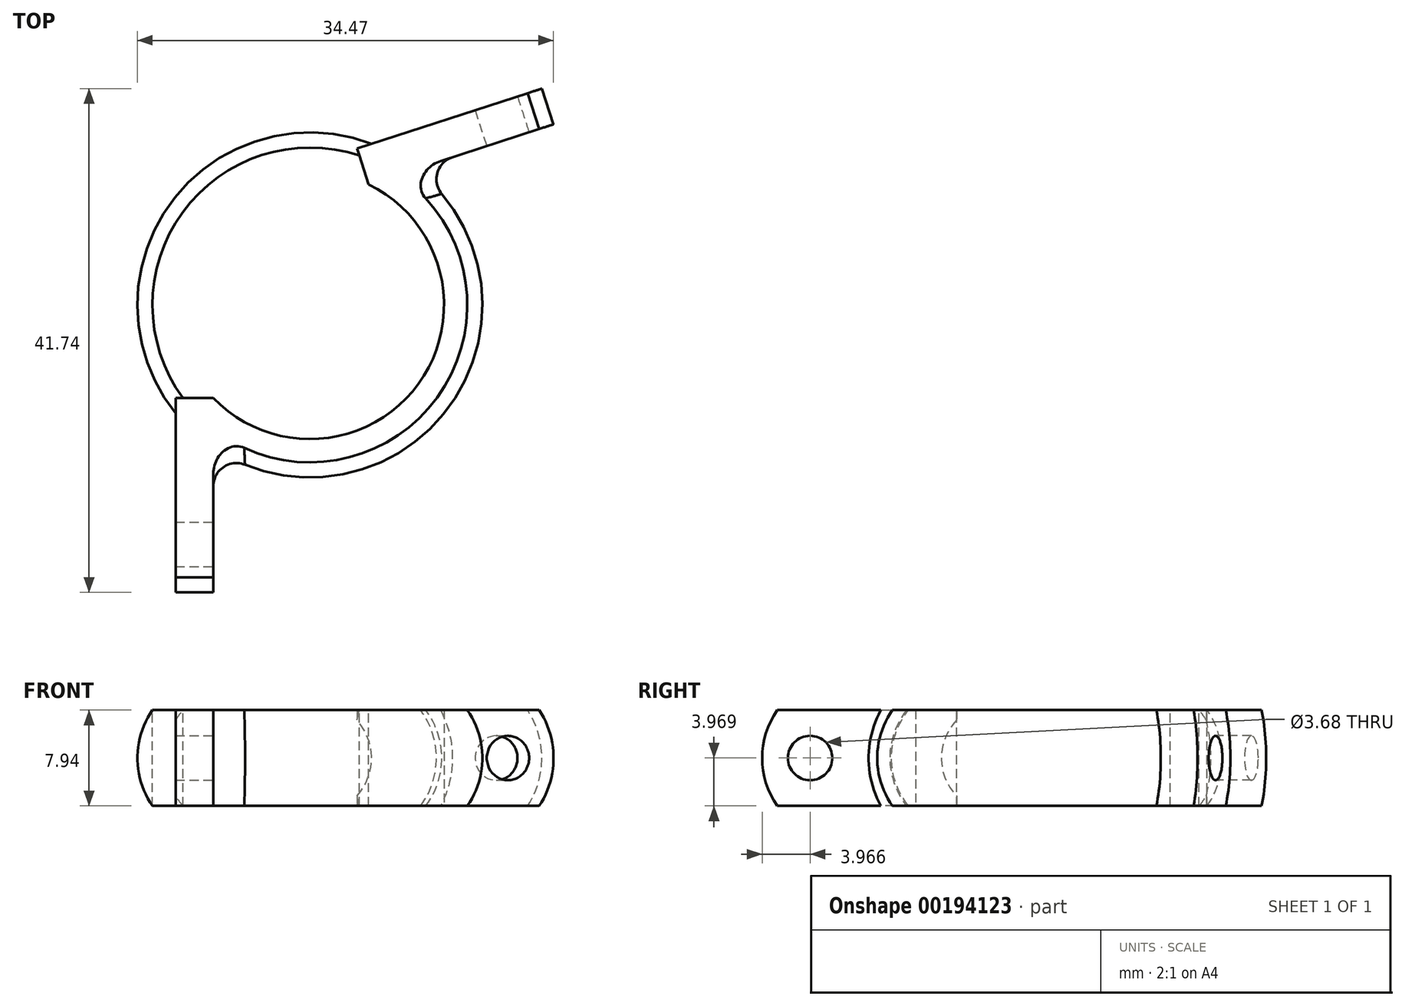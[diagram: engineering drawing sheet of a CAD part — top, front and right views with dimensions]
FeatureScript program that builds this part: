
annotation { "Feature Type Name" : "Feature", "Feature Type Description" : "" }
export const myFeature = defineFeature(function(context is Context, id is Id, definition is map)
    precondition{}
    {
        {
            var Q0;
            Q0=qCreatedBy(makeId("Top.planeOp"),FACE);
            var sketch = newSketch(context, id + "F0", { "sketchPlane" : qUnion([Q0])});
            skCircle(sketch, "E0", {"center": v(0, 0) * mm, "radius": 11.11 * mm, "construction": true});
            skLineSegment(sketch, "E1", {"start": v(-11.11, -27.21) * mm, "end": v(-11.11, 8.07) * mm, "construction": true});
            skLineSegment(sketch, "E2", {"start": v(-11.11, 8.07) * mm, "end": v(23.14, 19.2) * mm, "construction": true});
            skSolve(sketch);
        }
        {
            var Q0;
            Q0=qCreatedBy(makeId("Front.planeOp"),FACE);
            var sketch = newSketch(context, id + "F1", { "sketchPlane" : qUnion([Q0])});
            skLineSegment(sketch, "E3", {"start": v(-13.04, 0) * mm, "end": v(-11.11, 0) * mm});
            skLineSegment(sketch, "E4", {"start": v(-11.11, 0) * mm, "end": v(-11.11, 7.94) * mm});
            skLineSegment(sketch, "E5", {"start": v(-11.11, 7.94) * mm, "end": v(-13.04, 7.94) * mm});
            skArc(sketch, "E6", {"start": v(-13.04, 7.94) * mm, "mid": v(-14.29, 3.97) * mm, "end": v(-13.04, 0) * mm});
            skLineSegment(sketch, "E7", {"start": v(-13.04, 0) * mm, "end": v(-15.82, 3.97) * mm, "construction": true});
            skLineSegment(sketch, "E8", {"start": v(-13.04, 7.94) * mm, "end": v(-13.04, 0) * mm, "construction": true});
            skLineSegment(sketch, "E9", {"start": v(0, 0) * mm, "end": v(0, 7.94) * mm, "construction": true});
            skSolve(sketch);
        }
        {
            var Q0;
            Q0=makeQuery(id+"F1.imprint","IMPRINT",FACE,{"disambiguationData":[TD([[makeQuery(id+"F1.imprint","IMPRINT",EDGE,{"derivedFrom":sQuery(id+"F1.wireOp",EDGE,"E3")}),1.0]])]});
            var Q1;
            Q1=sQuery(id+"F1.wireOp",EDGE,"E9");
            revolve(context, id + "F2", {"entities" : qUnion([Q0]), "axis" : qUnion([Q1]), "revolveType" : RevolveType.FULL});
        }
        {
            var Q0;
            Q0=makeQuery(id+"F2.opRevolve","SWEPT_FACE",FACE,{"disambiguationData":[OSD([sQuery(id+"F1.wireOp",EDGE,"E5")])]});
            var sketch = newSketch(context, id + "F3", { "sketchPlane" : qUnion([Q0])});
            skLineSegment(sketch, "E10", {"start": v(-6.53, -9) * mm, "end": v(6.53, 9) * mm, "construction": true});
            skLineSegment(sketch, "E11", {"start": v(0, 0) * mm, "end": v(-11.11, 8.07) * mm, "construction": true});
            skLineSegment(sketch, "E12", {"start": v(4.87, 9.99) * mm, "end": v(0, 0) * mm, "construction": true});
            skLineSegment(sketch, "E13", {"start": v(0, 0) * mm, "end": v(-8, -7.72) * mm, "construction": true});
            skArc(sketch, "E14", {"start": v(-8, -7.72) * mm, "mid": v(-9, 6.53) * mm, "end": v(4.87, 9.99) * mm});
            skArc(sketch, "E15", {"start": v(-10.28, -9.92) * mm, "mid": v(-11.56, 8.4) * mm, "end": v(6.26, 12.84) * mm});
            skLineSegment(sketch, "E16", {"start": v(6.26, 12.84) * mm, "end": v(4.87, 9.99) * mm});
            skLineSegment(sketch, "E17", {"start": v(-8, -7.72) * mm, "end": v(-10.28, -9.92) * mm});
            skSolve(sketch);
        }
        {
            var Q0;
            {var subQ0=sQuery(id+"F3.wireOp",EDGE,"E15");Q0=makeQuery(id+"F3.imprint","IMPRINT",FACE,{"disambiguationData":[TD([[makeQuery(id+"F3.imprint","IMPRINT",EDGE,{"derivedFrom":subQ0}),-1.0]])]});}
            var Q1;
            {var subQ0=sQuery(id+"F3.wireOp",EDGE,"E14");Q1=makeQuery(id+"F3.imprint","IMPRINT",FACE,{"disambiguationData":[TD([[makeQuery(id+"F3.imprint","IMPRINT",EDGE,{"derivedFrom":subQ0}),1.0]])]});}
            extrude(context, id + "F4", {"entities" : qUnion([Q0, Q1]), "operationType" : NewBodyOperationType.REMOVE, "endBound" : BoundingType.UP_TO_NEXT, "oppositeDirection" : true, "depth" : 25.4 * mm});
        }
        {
            var Q0;
            Q0=qCreatedBy(makeId("Top.planeOp"),FACE);
            var sketch = newSketch(context, id + "F5", { "sketchPlane" : qUnion([Q0])});
            skCircle(sketch, "E18", {"center": v(0, 0) * mm, "radius": 14.29 * mm, "construction": true});
            skLineSegment(sketch, "E19.bottom", {"start": v(-11.11, -7.72) * mm, "end": v(-8, -7.72) * mm});
            skLineSegment(sketch, "E19.top", {"start": v(-11.11, -23.81) * mm, "end": v(-8, -23.81) * mm});
            skLineSegment(sketch, "E19.left", {"start": v(-11.11, -7.72) * mm, "end": v(-11.11, -23.81) * mm});
            skLineSegment(sketch, "E19.right", {"start": v(-8, -7.72) * mm, "end": v(-8, -23.81) * mm});
            skLineSegment(sketch, "E20", {"start": v(19.21, 17.93) * mm, "end": v(3.9, 12.95) * mm});
            skLineSegment(sketch, "E21", {"start": v(3.9, 12.95) * mm, "end": v(4.87, 9.99) * mm});
            skLineSegment(sketch, "E22", {"start": v(4.87, 9.99) * mm, "end": v(20.18, 14.96) * mm});
            skLineSegment(sketch, "E23", {"start": v(20.18, 14.96) * mm, "end": v(19.21, 17.93) * mm});
            skLineSegment(sketch, "E24", {"start": v(13.59, 4.42) * mm, "end": v(11.12, 12.02) * mm, "construction": true});
            skLineSegment(sketch, "E25", {"start": v(0, -14.29) * mm, "end": v(-8, -14.29) * mm, "construction": true});
            skLineSegment(sketch, "E26", {"start": v(0, -14.29) * mm, "end": v(0, -13.04) * mm, "construction": true});
            skLineSegment(sketch, "E27", {"start": v(13.59, 4.42) * mm, "end": v(12.4, 4.03) * mm, "construction": true});
            skSolve(sketch);
        }
        {
            var Q0;
            Q0=makeQuery(id+"F5.imprint","IMPRINT",FACE,{"disambiguationData":[TD([[makeQuery(id+"F5.imprint","IMPRINT",EDGE,{"derivedFrom":sQuery(id+"F5.wireOp",EDGE,"E19.bottom")}),-1.0]])]});
            var Q1;
            Q1=makeQuery(id+"F5.imprint","IMPRINT",FACE,{"disambiguationData":[TD([[makeQuery(id+"F5.imprint","IMPRINT",EDGE,{"derivedFrom":sQuery(id+"F5.wireOp",EDGE,"E20")}),1.0]])]});
            var Q2;
            Q2=makeQuery(id+"F2.opRevolve","SWEPT_FACE",FACE,{"disambiguationData":[OSD([sQuery(id+"F1.wireOp",EDGE,"E5")])]});
            extrude(context, id + "F6", {"entities" : qUnion([Q0, Q1]), "operationType" : NewBodyOperationType.ADD, "endBound" : BoundingType.UP_TO_SURFACE, "endBoundEntityFace" : qUnion([Q2]), "depth" : 25.4 * mm});
        }
        {
            var Q0;
            Q0=makeQuery(id+"F6.opExtrude","SWEPT_FACE",FACE,{"disambiguationData":[OSD([sQuery(id+"F5.wireOp",EDGE,"E19.right")])]});
            var sketch = newSketch(context, id + "F7", { "sketchPlane" : qUnion([Q0])});
            skCircle(sketch, "E28", {"center": v(-19.84, 3.97) * mm, "radius": 3.97 * mm, "construction": true});
            skCircle(sketch, "E29", {"center": v(-19.84, 3.97) * mm, "radius": 1.84 * mm});
            skLineSegment(sketch, "E30", {"start": v(-13.04, 0) * mm, "end": v(-13.04, 7.94) * mm, "construction": true});
            skLineSegment(sketch, "E31", {"start": v(-14.29, 7.94) * mm, "end": v(-14.29, 0) * mm, "construction": true});
            skArc(sketch, "E32", {"start": v(-13.04, 7.94) * mm, "mid": v(-14.29, 3.97) * mm, "end": v(-13.04, 0) * mm});
            skArc(sketch, "E33", {"start": v(-10.3, 7.94) * mm, "mid": v(-11.84, 3.97) * mm, "end": v(-10.3, 0) * mm});
            skArc(sketch, "E34", {"start": v(-22.56, 7.94) * mm, "mid": v(-23.81, 3.97) * mm, "end": v(-22.56, 0) * mm});
            skLineSegment(sketch, "E35", {"start": v(-10.3, 7.94) * mm, "end": v(-13.04, 7.94) * mm});
            skLineSegment(sketch, "E36", {"start": v(-10.3, 0) * mm, "end": v(-13.04, 0) * mm});
            skSolve(sketch);
        }
        {
            var Q0;
            {var subQ0=sQuery(id+"F7.wireOp",EDGE,"E34");var subQ1=sQuery(id+"F5.wireOp",EDGE,"E19.right");var subQ2=makeQuery(id+"F6.opExtrude","CAP_EDGE",EDGE,{"disambiguationData":[OSD([subQ1])],"isStart":false});var subQ3=makeQuery(id+"F7.imprint","INTERSECT",VERTEX,{"derivedFrom":[subQ2,subQ0]});Q0=makeQuery(id+"F7.imprint","IMPRINT",FACE,{"disambiguationData":[TD([[makeQuery(id+"F7.imprint","IMPRINT",EDGE,{"disambiguationData":[TD([[subQ3,-1.0]])],"derivedFrom":subQ0}),-1.0]])]});}
            var Q1;
            {var subQ0=sQuery(id+"F7.wireOp",EDGE,"E34");var subQ1=sQuery(id+"F5.wireOp",EDGE,"E19.right");var subQ2=makeQuery(id+"F6.opExtrude","CAP_EDGE",EDGE,{"disambiguationData":[OSD([subQ1])],"isStart":true});var subQ3=makeQuery(id+"F7.imprint","INTERSECT",VERTEX,{"derivedFrom":[subQ2,subQ0]});Q1=makeQuery(id+"F7.imprint","IMPRINT",FACE,{"disambiguationData":[TD([[makeQuery(id+"F7.imprint","IMPRINT",EDGE,{"disambiguationData":[TD([[subQ3,1.0]])],"derivedFrom":subQ0}),-1.0]])]});}
            var Q2;
            Q2=makeQuery(id+"F7.imprint","IMPRINT",FACE,{"disambiguationData":[TD([[makeQuery(id+"F7.imprint","IMPRINT",EDGE,{"derivedFrom":sQuery(id+"F7.wireOp",EDGE,"E29")}),1.0]])]});
            extrude(context, id + "F8", {"entities" : qUnion([Q0, Q1, Q2]), "operationType" : NewBodyOperationType.REMOVE, "endBound" : BoundingType.UP_TO_NEXT, "oppositeDirection" : true, "depth" : 25.4 * mm});
        }
        {
            var Q0;
            Q0=makeQuery(id+"F6.opExtrude","SWEPT_FACE",FACE,{"disambiguationData":[OSD([sQuery(id+"F5.wireOp",EDGE,"E22")])]});
            var sketch = newSketch(context, id + "F9", { "sketchPlane" : qUnion([Q0])});
            skLineSegment(sketch, "E37", {"start": v(14.29, 0) * mm, "end": v(14.29, 7.94) * mm, "construction": true});
            skLineSegment(sketch, "E38", {"start": v(13.04, 0) * mm, "end": v(13.04, 7.94) * mm, "construction": true});
            skArc(sketch, "E39", {"start": v(13.04, 0) * mm, "mid": v(14.29, 3.97) * mm, "end": v(13.04, 7.94) * mm, "construction": true});
            skArc(sketch, "E40", {"start": v(22.56, 0) * mm, "mid": v(23.81, 3.97) * mm, "end": v(22.56, 7.94) * mm});
            skCircle(sketch, "E41", {"center": v(19.84, 3.97) * mm, "radius": 3.97 * mm, "construction": true});
            skCircle(sketch, "E42", {"center": v(19.84, 3.97) * mm, "radius": 1.84 * mm});
            skLineSegment(sketch, "E43", {"start": v(-13.73, 5.81) * mm, "end": v(19.84, 5.81) * mm, "construction": true});
            skLineSegment(sketch, "E44", {"start": v(19.84, 5.81) * mm, "end": v(19.84, 3.97) * mm, "construction": true});
            skSolve(sketch);
        }
        {
            var Q0;
            Q0=makeQuery(id+"F9.imprint","IMPRINT",FACE,{"disambiguationData":[TD([[makeQuery(id+"F9.imprint","IMPRINT",EDGE,{"derivedFrom":sQuery(id+"F9.wireOp",EDGE,"E42")}),1.0]])]});
            var Q1;
            {var subQ0=sQuery(id+"F9.wireOp",EDGE,"E40");var subQ1=sQuery(id+"F5.wireOp",EDGE,"E22");var subQ2=makeQuery(id+"F6.opExtrude","CAP_EDGE",EDGE,{"disambiguationData":[OSD([subQ1])],"isStart":false});var subQ3=makeQuery(id+"F9.imprint","INTERSECT",VERTEX,{"derivedFrom":[subQ2,subQ0]});Q1=makeQuery(id+"F9.imprint","IMPRINT",FACE,{"disambiguationData":[TD([[makeQuery(id+"F9.imprint","IMPRINT",EDGE,{"disambiguationData":[TD([[subQ3,1.0]])],"derivedFrom":subQ0}),-1.0]])]});}
            var Q2;
            {var subQ0=sQuery(id+"F9.wireOp",EDGE,"E40");var subQ1=sQuery(id+"F5.wireOp",EDGE,"E22");var subQ2=makeQuery(id+"F6.opExtrude","CAP_EDGE",EDGE,{"disambiguationData":[OSD([subQ1])],"isStart":true});var subQ3=makeQuery(id+"F9.imprint","INTERSECT",VERTEX,{"derivedFrom":[subQ2,subQ0]});Q2=makeQuery(id+"F9.imprint","IMPRINT",FACE,{"disambiguationData":[TD([[makeQuery(id+"F9.imprint","IMPRINT",EDGE,{"disambiguationData":[TD([[subQ3,-1.0]])],"derivedFrom":subQ0}),-1.0]])]});}
            extrude(context, id + "F10", {"entities" : qUnion([Q0, Q1, Q2]), "operationType" : NewBodyOperationType.REMOVE, "endBound" : BoundingType.UP_TO_NEXT, "oppositeDirection" : true, "depth" : 25.4 * mm});
        }
        {
            var Q0;
            Q0=makeQuery(id+"F6.boolean.opBoolean","INTERSECT",EDGE,{"derivedFrom":[makeQuery(id+"F2.opRevolve","SWEPT_FACE",FACE,{"disambiguationData":[OSD([sQuery(id+"F1.wireOp",EDGE,"E6")])]}),makeQuery(id+"F6.opExtrude","SWEPT_FACE",FACE,{"disambiguationData":[OSD([sQuery(id+"F5.wireOp",EDGE,"E19.right")])]})]});
            var Q1;
            Q1=makeQuery(id+"F6.boolean.opBoolean","INTERSECT",EDGE,{"derivedFrom":[makeQuery(id+"F2.opRevolve","SWEPT_FACE",FACE,{"disambiguationData":[OSD([sQuery(id+"F1.wireOp",EDGE,"E6")])]}),makeQuery(id+"F6.opExtrude","SWEPT_FACE",FACE,{"disambiguationData":[OSD([sQuery(id+"F5.wireOp",EDGE,"E22")])]})]});
            fillet(context, id + "F11", {"entities" : qUnion([Q0, Q1]), "radius" : 1.9 * mm, "tangentPropagation" : true, "allowEdgeOverflow" : false});
        }
    });
